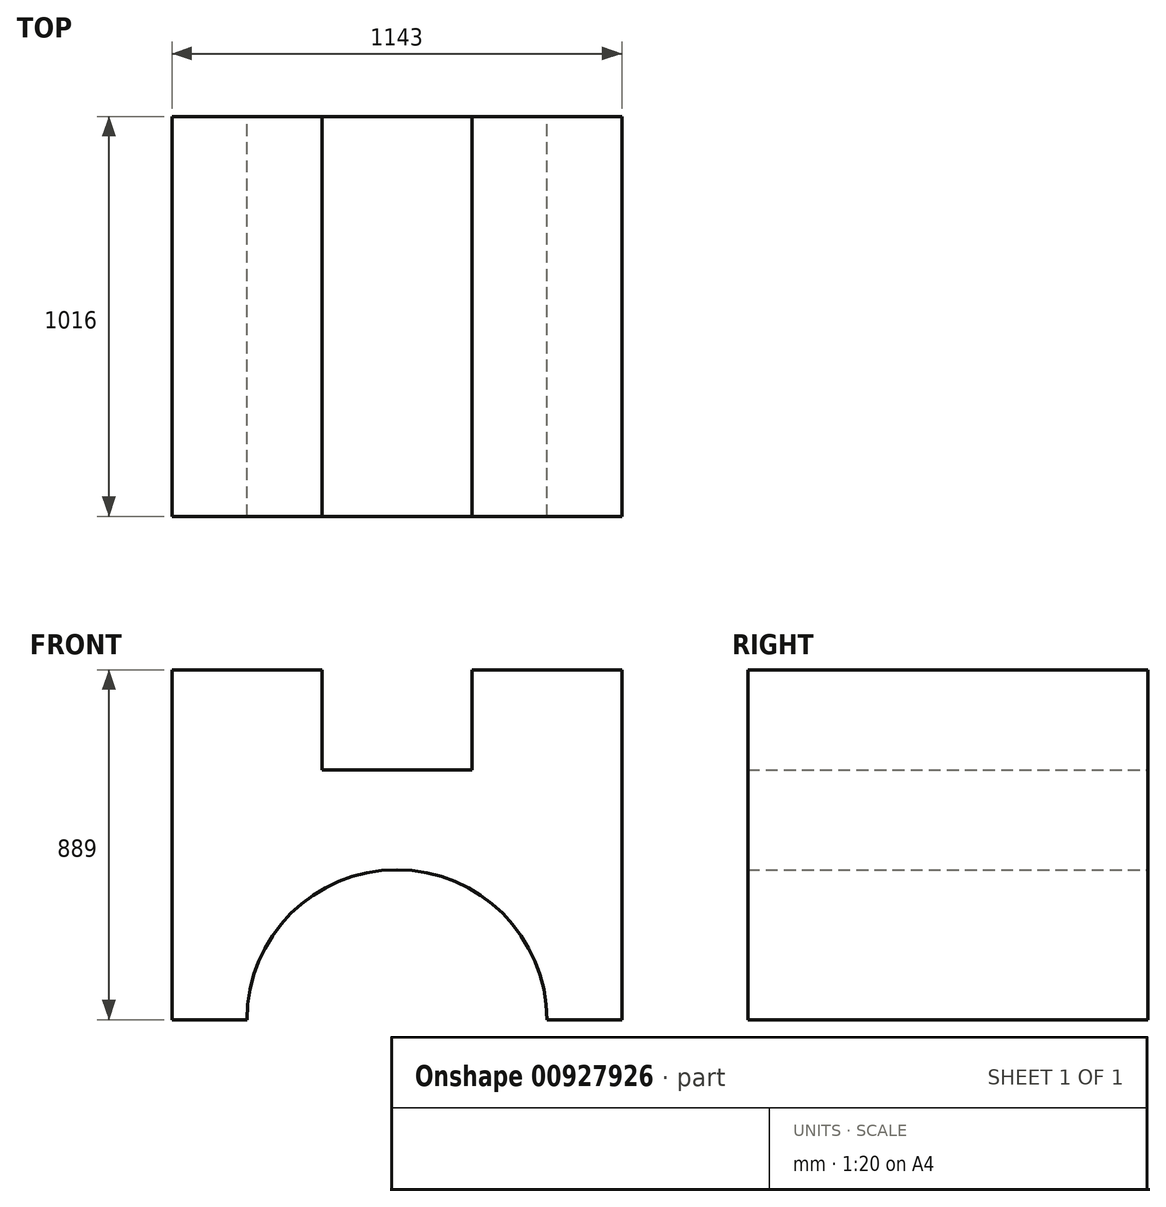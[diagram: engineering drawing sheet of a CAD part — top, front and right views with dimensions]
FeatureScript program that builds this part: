
annotation { "Feature Type Name" : "Feature", "Feature Type Description" : "" }
export const myFeature = defineFeature(function(context is Context, id is Id, definition is map)
    precondition{}
    {
        {
            var Q0;
            Q0=qCreatedBy(makeId("Front.planeOp"),FACE);
            var sketch = newSketch(context, id + "F0", { "sketchPlane" : qUnion([Q0])});
            skLineSegment(sketch, "E0.bottom", {"start": v(-555.16, 248.66) * mm, "end": v(-174.16, 248.66) * mm});
            skLineSegment(sketch, "E0.top", {"start": v(-555.16, -640.34) * mm, "end": v(-364.66, -640.34) * mm});
            skLineSegment(sketch, "E0.left", {"start": v(-555.16, 248.66) * mm, "end": v(-555.16, -640.34) * mm});
            skLineSegment(sketch, "E0.right", {"start": v(587.84, 248.66) * mm, "end": v(587.84, -640.34) * mm});
            skArc(sketch, "E1", {"start": v(397.34, -640.34) * mm, "mid": v(16.34, -259.34) * mm, "end": v(-364.66, -640.34) * mm});
            skLineSegment(sketch, "E2.top", {"start": v(-174.16, -5.95) * mm, "end": v(206.84, -5.95) * mm});
            skLineSegment(sketch, "E2.left", {"start": v(-174.16, 248.66) * mm, "end": v(-174.16, -5.95) * mm});
            skLineSegment(sketch, "E2.right", {"start": v(206.84, 248.66) * mm, "end": v(206.84, -5.95) * mm});
            skLineSegment(sketch, "E3.trimOffspring", {"start": v(206.84, 248.66) * mm, "end": v(587.84, 248.66) * mm});
            skLineSegment(sketch, "E4.trimOffspring", {"start": v(397.34, -640.34) * mm, "end": v(587.84, -640.34) * mm});
            skSolve(sketch);
        }
        {
            var Q0;
            Q0 = qSketchRegion(id + "F0", true);
            extrude(context, id + "F1", {"entities" : qUnion([Q0]), "depth" : 1016 * mm, "offsetDistance" : 25.4 * mm});
        }
    });
